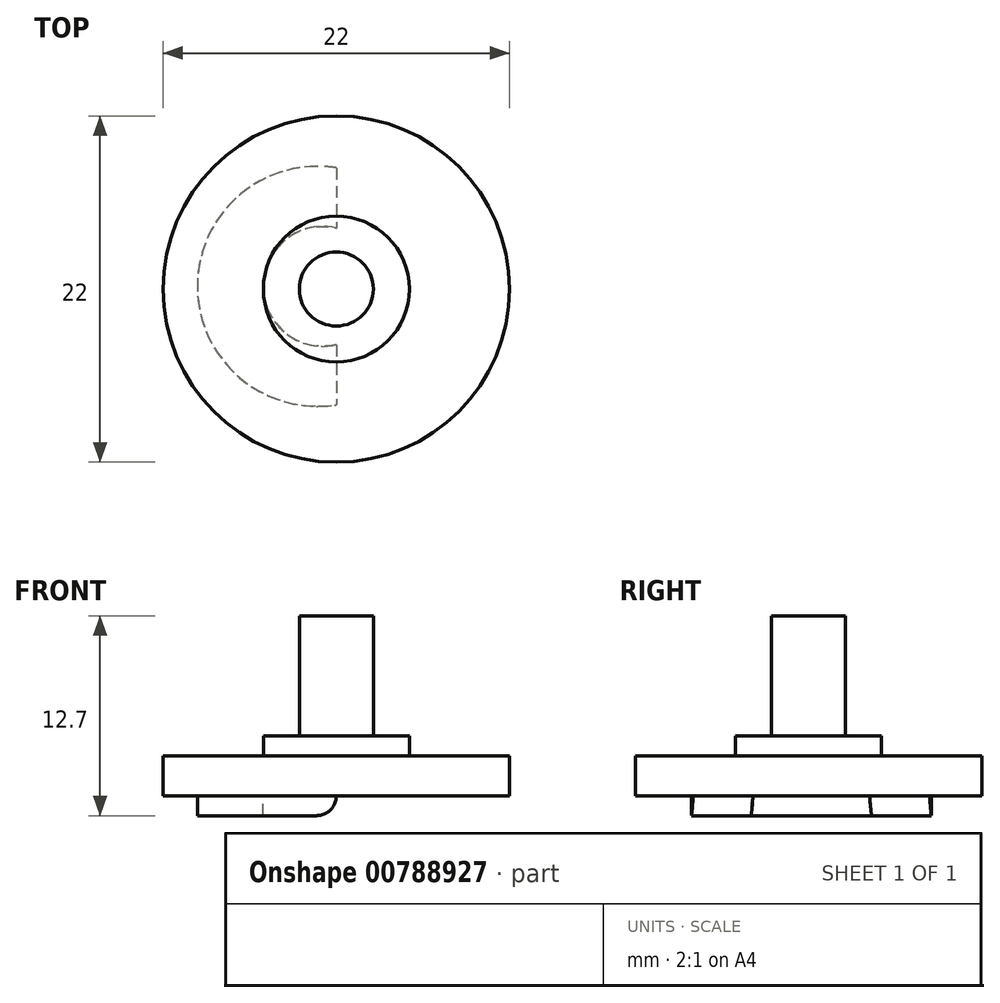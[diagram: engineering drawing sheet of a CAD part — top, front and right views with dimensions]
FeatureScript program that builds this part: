
annotation { "Feature Type Name" : "Feature", "Feature Type Description" : "" }
export const myFeature = defineFeature(function(context is Context, id is Id, definition is map)
    precondition{}
    {
        {
            var Q0;
            Q0=qCreatedBy(makeId("Top.planeOp"),FACE);
            var sketch = newSketch(context, id + "F0", { "sketchPlane" : qUnion([Q0])});
            skCircle(sketch, "E0", {"center": v(0, 0) * mm, "radius": 11 * mm});
            skCircle(sketch, "E1", {"center": v(0, 0) * mm, "radius": 4.64 * mm});
            skCircle(sketch, "E2", {"center": v(0, 0) * mm, "radius": 2.35 * mm});
            skSolve(sketch);
        }
        {
            var Q0;
            Q0=makeQuery(id+"F0.imprint","IMPRINT",FACE,{"disambiguationData":[TD([[makeQuery(id+"F0.imprint","IMPRINT",EDGE,{"derivedFrom":sQuery(id+"F0.wireOp",EDGE,"E2")}),1.0]])]});
            extrude(context, id + "F1", {"entities" : qUnion([Q0]), "depth" : 11.43 * mm, "offsetDistance" : 25.4 * mm});
        }
        {
            var Q0;
            Q0=makeQuery(id+"F0.imprint","IMPRINT",FACE,{"disambiguationData":[TD([[makeQuery(id+"F0.imprint","IMPRINT",EDGE,{"derivedFrom":sQuery(id+"F0.wireOp",EDGE,"E1")}),1.0]])]});
            extrude(context, id + "F2", {"entities" : qUnion([Q0]), "operationType" : NewBodyOperationType.ADD, "depth" : 3.8 * mm, "offsetDistance" : 25.4 * mm});
        }
        {
            var Q0;
            Q0=makeQuery(id+"F0.imprint","IMPRINT",FACE,{"disambiguationData":[TD([[makeQuery(id+"F0.imprint","IMPRINT",EDGE,{"derivedFrom":sQuery(id+"F0.wireOp",EDGE,"E0")}),1.0]])]});
            extrude(context, id + "F3", {"entities" : qUnion([Q0]), "operationType" : NewBodyOperationType.ADD, "depth" : 2.54 * mm, "offsetDistance" : 25.4 * mm});
        }
        {
            var Q0;
            Q0=makeQuery(id+"F0.imprint","IMPRINT",FACE,{"disambiguationData":[TD([[makeQuery(id+"F0.imprint","IMPRINT",EDGE,{"derivedFrom":sQuery(id+"F0.wireOp",EDGE,"E0")}),1.0]])]});
            var sketch = newSketch(context, id + "F4", { "sketchPlane" : qUnion([Q0])});
            skArc(sketch, "E3", {"start": v(0, 7.7) * mm, "mid": v(-8.83, 0.17) * mm, "end": v(0, -7.35) * mm});
            skArc(sketch, "E4", {"start": v(0, 3.89) * mm, "mid": v(-4.64, 0.17) * mm, "end": v(0, -3.55) * mm});
            skLineSegment(sketch, "E5", {"start": v(0, -3.55) * mm, "end": v(0, -7.35) * mm});
            skLineSegment(sketch, "E6", {"start": v(0, 7.7) * mm, "end": v(0, 3.89) * mm});
            skSolve(sketch);
        }
        {
            var Q0;
            Q0 = qSketchRegion(id + "F4", true);
            extrude(context, id + "F5", {"entities" : qUnion([Q0]), "operationType" : NewBodyOperationType.ADD, "oppositeDirection" : true, "depth" : 1.27 * mm, "offsetDistance" : 25.4 * mm});
        }
        {
            var Q0;
            Q0=makeQuery(id+"F5.opExtrude","CAP_EDGE",EDGE,{"disambiguationData":[OSD([sQuery(id+"F4.wireOp",EDGE,"E6")])],"isStart":false});
            var Q1;
            Q1=makeQuery(id+"F5.opExtrude","CAP_EDGE",EDGE,{"disambiguationData":[OSD([sQuery(id+"F4.wireOp",EDGE,"E5")])],"isStart":false});
            fillet(context, id + "F6", {"entities" : qUnion([Q0, Q1]), "radius" : 1.27 * mm, "tangentPropagation" : true, "allowEdgeOverflow" : false});
        }
    });
